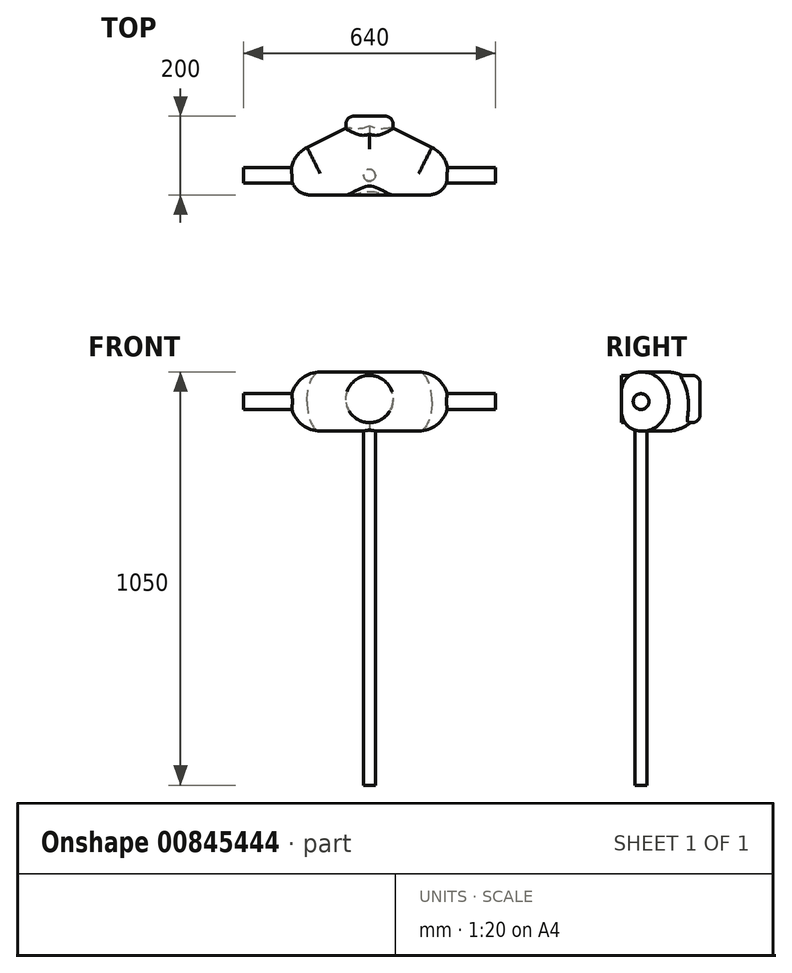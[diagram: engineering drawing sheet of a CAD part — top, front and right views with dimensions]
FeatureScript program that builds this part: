
annotation { "Feature Type Name" : "Feature", "Feature Type Description" : "" }
export const myFeature = defineFeature(function(context is Context, id is Id, definition is map)
    precondition{}
    {
        {
            var Q0;
            Q0=qCreatedBy(makeId("Top.planeOp"),FACE);
            var sketch = newSketch(context, id + "F0", { "sketchPlane" : qUnion([Q0])});
            skLineSegment(sketch, "E0.top", {"start": v(-200, 0) * mm, "end": v(200, 0) * mm});
            skLineSegment(sketch, "E0.left", {"start": v(-200, 100) * mm, "end": v(-200, 0) * mm});
            skLineSegment(sketch, "E0.right", {"start": v(200, 100) * mm, "end": v(200, 0) * mm});
            skLineSegment(sketch, "E1", {"start": v(-200, 100) * mm, "end": v(0, 200) * mm});
            skLineSegment(sketch, "E2", {"start": v(0, 200) * mm, "end": v(200, 100) * mm});
            skPoint(sketch, "E3.orphan", {"position": v(-200, 200) * mm});
            skPoint(sketch, "E4.orphan", {"position": v(200, 200) * mm});
            skSolve(sketch);
        }
        {
            var Q0;
            Q0=makeQuery(id+"F0.imprint","IMPRINT",FACE,{"disambiguationData":[TD([[makeQuery(id+"F0.imprint","IMPRINT",EDGE,{"derivedFrom":sQuery(id+"F0.wireOp",EDGE,"E0.top")}),1.0]])]});
            extrude(context, id + "F1", {"entities" : qUnion([Q0]), "depth" : 150 * mm, "offsetDistance" : 25 * mm});
        }
        {
            var Q0;
            Q0=makeQuery(id+"F1.opExtrude","SWEPT_FACE",FACE,{"disambiguationData":[OSD([sQuery(id+"F0.wireOp",EDGE,"E0.right")])]});
            var sketch = newSketch(context, id + "F2", { "sketchPlane" : qUnion([Q0])});
            skCircle(sketch, "E5", {"center": v(50, 75) * mm, "radius": 20 * mm});
            skSolve(sketch);
        }
        {
            var Q0;
            Q0=makeQuery(id+"F2.imprint","IMPRINT",FACE,{"disambiguationData":[TD([[makeQuery(id+"F2.imprint","IMPRINT",EDGE,{"derivedFrom":sQuery(id+"F2.wireOp",EDGE,"E5")}),1.0]])]});
            extrude(context, id + "F3", {"entities" : qUnion([Q0]), "operationType" : NewBodyOperationType.ADD, "depth" : 120 * mm, "offsetDistance" : 25 * mm});
        }
        {
            var Q0;
            Q0=makeQuery(id+"F1.opExtrude","SWEPT_FACE",FACE,{"disambiguationData":[OSD([sQuery(id+"F0.wireOp",EDGE,"E0.left")])]});
            var sketch = newSketch(context, id + "F4", { "sketchPlane" : qUnion([Q0])});
            skCircle(sketch, "E6", {"center": v(-50, 75) * mm, "radius": 20 * mm});
            skSolve(sketch);
        }
        {
            var Q0;
            Q0=makeQuery(id+"F4.imprint","IMPRINT",FACE,{"disambiguationData":[TD([[makeQuery(id+"F4.imprint","IMPRINT",EDGE,{"derivedFrom":sQuery(id+"F4.wireOp",EDGE,"E6")}),1.0]])]});
            extrude(context, id + "F5", {"entities" : qUnion([Q0]), "operationType" : NewBodyOperationType.ADD, "depth" : 120 * mm, "offsetDistance" : 25 * mm});
        }
        {
            var Q0;
            Q0=makeQuery(id+"F1.opExtrude","CAP_EDGE",EDGE,{"disambiguationData":[OSD([sQuery(id+"F0.wireOp",EDGE,"E2")])],"isStart":false});
            var Q1;
            Q1=makeQuery(id+"F1.opExtrude","CAP_EDGE",EDGE,{"disambiguationData":[OSD([sQuery(id+"F0.wireOp",EDGE,"E1")])],"isStart":false});
            fillet(context, id + "F6", {"entities" : qUnion([Q0, Q1]), "radius" : 75 * mm, "tangentPropagation" : true, "allowEdgeOverflow" : false});
        }
        {
            var Q0;
            Q0=qCreatedBy(makeId("Top.planeOp"),FACE);
            cPlane(context, id + "F7", {"entities" : qUnion([Q0]), "cplaneType" : CPlaneType.OFFSET, "offset" : 75 * mm, "width" : 150 * mm, "height" : 150 * mm});
        }
        {
            var Q0;
            Q0=qCreatedBy(id+"F7.planeOp",FACE);
            var sketch = newSketch(context, id + "F8", { "sketchPlane" : qUnion([Q0])});
            skFitSpline(sketch, "E7", {"points": [v(201.23, 72.54) * mm, v(229.73, 89.81) * mm, v(272.48, 86.79) * mm, v(312.64, 95.86) * mm], "startDerivative": vector(84.68, 74.54) * mm, "endDerivative": vector(113.81, 40.36) * mm});
            skSolve(sketch);
        }
        {
            var Q0;
            Q0=makeQuery(id+"F1.opExtrude","SWEPT_FACE",FACE,{"disambiguationData":[OSD([sQuery(id+"F0.wireOp",EDGE,"E0.right")])]});
            var sketch = newSketch(context, id + "F9", { "sketchPlane" : qUnion([Q0])});
            skCircle(sketch, "E8", {"center": v(72.54, 75) * mm, "radius": 2.5 * mm});
            skSolve(sketch);
        }
        {
            var Q0;
            Q0=makeQuery(id+"F1.opExtrude","SWEPT_EDGE",EDGE,{"disambiguationData":[OSD([sQuery(id+"F0.wireOp",EDGE,"E0.right"),sQuery(id+"F0.wireOp",EDGE,"E2")])]});
            var Q1;
            Q1=makeQuery(id+"F1.opExtrude","SWEPT_EDGE",EDGE,{"disambiguationData":[OSD([sQuery(id+"F0.wireOp",EDGE,"E0.left"),sQuery(id+"F0.wireOp",EDGE,"E1")])]});
            fillet(context, id + "F10", {"entities" : qUnion([Q0, Q1]), "radius" : 75 * mm, "tangentPropagation" : true, "allowEdgeOverflow" : false});
        }
        {
            var Q0;
            Q0=makeQuery(id+"F1.opExtrude","CAP_FACE",FACE,{"disambiguationData":[OSD([sQuery(id+"F0.wireOp",EDGE,"E0.top"),sQuery(id+"F0.wireOp",EDGE,"E0.left"),sQuery(id+"F0.wireOp",EDGE,"E0.right"),sQuery(id+"F0.wireOp",EDGE,"E1"),sQuery(id+"F0.wireOp",EDGE,"E2")])],"isStart":true});
            var sketch = newSketch(context, id + "F11", { "sketchPlane" : qUnion([Q0])});
            skCircle(sketch, "E9", {"center": v(0, -50) * mm, "radius": 15 * mm});
            skSolve(sketch);
        }
        {
            var Q0;
            Q0=makeQuery(id+"F11.imprint","IMPRINT",FACE,{"disambiguationData":[TD([[makeQuery(id+"F11.imprint","IMPRINT",EDGE,{"derivedFrom":sQuery(id+"F11.wireOp",EDGE,"E9")}),1.0]])]});
            extrude(context, id + "F12", {"entities" : qUnion([Q0]), "operationType" : NewBodyOperationType.ADD, "depth" : 900 * mm, "offsetDistance" : 25 * mm});
        }
        {
            var Q0;
            Q0=makeQuery(id+"F1.opExtrude","CAP_EDGE",EDGE,{"disambiguationData":[OSD([sQuery(id+"F0.wireOp",EDGE,"E2")])],"isStart":true});
            var Q1;
            {var subQ0=sQuery(id+"F0.wireOp",EDGE,"E2");var subQ1=sQuery(id+"F0.wireOp",EDGE,"E0.right");Q1=makeQuery(id+"F10.opFillet","BLEND_EDGE",EDGE,{"blendedFrom":[makeQuery(id+"F1.opExtrude","SWEPT_EDGE",EDGE,{"disambiguationData":[OSD([subQ1,subQ0])]}),makeQuery(id+"F1.opExtrude","CAP_FACE",FACE,{"disambiguationData":[OSD([sQuery(id+"F0.wireOp",EDGE,"E0.top"),sQuery(id+"F0.wireOp",EDGE,"E0.left"),subQ1,sQuery(id+"F0.wireOp",EDGE,"E1"),subQ0])],"isStart":true})],"blendedInto":[makeQuery(id+"F1.opExtrude","CAP_FACE",FACE,{"disambiguationData":[OSD([sQuery(id+"F0.wireOp",EDGE,"E0.top"),sQuery(id+"F0.wireOp",EDGE,"E0.left"),subQ1,sQuery(id+"F0.wireOp",EDGE,"E1"),subQ0])],"isStart":true})]});}
            var Q2;
            Q2=makeQuery(id+"F1.opExtrude","CAP_EDGE",EDGE,{"disambiguationData":[OSD([sQuery(id+"F0.wireOp",EDGE,"E0.right")])],"isStart":true});
            var Q3;
            Q3=makeQuery(id+"F1.opExtrude","CAP_EDGE",EDGE,{"disambiguationData":[OSD([sQuery(id+"F0.wireOp",EDGE,"E1")])],"isStart":true});
            var Q4;
            {var subQ0=sQuery(id+"F0.wireOp",EDGE,"E1");var subQ1=sQuery(id+"F0.wireOp",EDGE,"E0.left");Q4=makeQuery(id+"F10.opFillet","BLEND_EDGE",EDGE,{"blendedFrom":[makeQuery(id+"F1.opExtrude","SWEPT_EDGE",EDGE,{"disambiguationData":[OSD([subQ1,subQ0])]}),makeQuery(id+"F1.opExtrude","CAP_FACE",FACE,{"disambiguationData":[OSD([sQuery(id+"F0.wireOp",EDGE,"E0.top"),subQ1,sQuery(id+"F0.wireOp",EDGE,"E0.right"),subQ0,sQuery(id+"F0.wireOp",EDGE,"E2")])],"isStart":true})],"blendedInto":[makeQuery(id+"F1.opExtrude","CAP_FACE",FACE,{"disambiguationData":[OSD([sQuery(id+"F0.wireOp",EDGE,"E0.top"),subQ1,sQuery(id+"F0.wireOp",EDGE,"E0.right"),subQ0,sQuery(id+"F0.wireOp",EDGE,"E2")])],"isStart":true})]});}
            var Q5;
            Q5=makeQuery(id+"F1.opExtrude","CAP_EDGE",EDGE,{"disambiguationData":[OSD([sQuery(id+"F0.wireOp",EDGE,"E0.left")])],"isStart":true});
            fillet(context, id + "F13", {"entities" : qUnion([Q0, Q1, Q2, Q3, Q4, Q5]), "radius" : 75 * mm, "tangentPropagation" : true, "allowEdgeOverflow" : false});
        }
        {
            var Q0;
            Q0=makeQuery(id+"F1.opExtrude","CAP_EDGE",EDGE,{"disambiguationData":[OSD([sQuery(id+"F0.wireOp",EDGE,"E0.top")])],"isStart":false});
            var Q1;
            Q1=makeQuery(id+"F10.opFillet","BLEND_EDGE",EDGE,{"blendedFrom":[makeQuery(id+"F1.opExtrude","CAP_EDGE",EDGE,{"disambiguationData":[OSD([sQuery(id+"F0.wireOp",EDGE,"E0.right")])],"isStart":false}),makeQuery(id+"F1.opExtrude","SWEPT_FACE",FACE,{"disambiguationData":[OSD([sQuery(id+"F0.wireOp",EDGE,"E0.top")])]})],"blendedInto":[makeQuery(id+"F1.opExtrude","SWEPT_FACE",FACE,{"disambiguationData":[OSD([sQuery(id+"F0.wireOp",EDGE,"E0.top")])]})]});
            var Q2;
            Q2=makeQuery(id+"F13.opFillet","BLEND_EDGE",EDGE,{"blendedFrom":[makeQuery(id+"F1.opExtrude","CAP_EDGE",EDGE,{"disambiguationData":[OSD([sQuery(id+"F0.wireOp",EDGE,"E0.right")])],"isStart":true}),makeQuery(id+"F1.opExtrude","SWEPT_FACE",FACE,{"disambiguationData":[OSD([sQuery(id+"F0.wireOp",EDGE,"E0.top")])]})],"blendedInto":[makeQuery(id+"F1.opExtrude","SWEPT_FACE",FACE,{"disambiguationData":[OSD([sQuery(id+"F0.wireOp",EDGE,"E0.top")])]})]});
            var Q3;
            Q3=makeQuery(id+"F1.opExtrude","CAP_EDGE",EDGE,{"disambiguationData":[OSD([sQuery(id+"F0.wireOp",EDGE,"E0.top")])],"isStart":true});
            var Q4;
            Q4=makeQuery(id+"F13.opFillet","BLEND_EDGE",EDGE,{"blendedFrom":[makeQuery(id+"F1.opExtrude","CAP_EDGE",EDGE,{"disambiguationData":[OSD([sQuery(id+"F0.wireOp",EDGE,"E0.left")])],"isStart":true}),makeQuery(id+"F1.opExtrude","SWEPT_FACE",FACE,{"disambiguationData":[OSD([sQuery(id+"F0.wireOp",EDGE,"E0.top")])]})],"blendedInto":[makeQuery(id+"F1.opExtrude","SWEPT_FACE",FACE,{"disambiguationData":[OSD([sQuery(id+"F0.wireOp",EDGE,"E0.top")])]})]});
            var Q5;
            Q5=makeQuery(id+"F10.opFillet","BLEND_EDGE",EDGE,{"blendedFrom":[makeQuery(id+"F1.opExtrude","CAP_EDGE",EDGE,{"disambiguationData":[OSD([sQuery(id+"F0.wireOp",EDGE,"E0.left")])],"isStart":false}),makeQuery(id+"F1.opExtrude","SWEPT_FACE",FACE,{"disambiguationData":[OSD([sQuery(id+"F0.wireOp",EDGE,"E0.top")])]})],"blendedInto":[makeQuery(id+"F1.opExtrude","SWEPT_FACE",FACE,{"disambiguationData":[OSD([sQuery(id+"F0.wireOp",EDGE,"E0.top")])]})]});
            fillet(context, id + "F14", {"entities" : qUnion([Q0, Q1, Q2, Q3, Q4, Q5]), "radius" : 50 * mm, "tangentPropagation" : true, "allowEdgeOverflow" : false});
        }
        {
            var Q0;
            Q0=makeQuery(id+"F1.opExtrude","SWEPT_FACE",FACE,{"disambiguationData":[OSD([sQuery(id+"F0.wireOp",EDGE,"E0.top")])]});
            var sketch = newSketch(context, id + "F15", { "sketchPlane" : qUnion([Q0])});
            skCircle(sketch, "E10", {"center": v(0, 81.49) * mm, "radius": 59.99 * mm});
            skSolve(sketch);
        }
        {
            var Q0;
            Q0 = qSketchRegion(id + "F15", true);
            extrude(context, id + "F16", {"entities" : qUnion([Q0]), "operationType" : NewBodyOperationType.ADD, "oppositeDirection" : true, "depth" : 200 * mm, "offsetDistance" : 25 * mm});
        }
        {
            var Q0;
            Q0=makeQuery(id+"F16.opExtrude","CAP_FACE",FACE,{"disambiguationData":[OSD([sQuery(id+"F15.wireOp",EDGE,"E10")])],"isStart":false});
            fillet(context, id + "F17", {"entities" : qUnion([Q0]), "radius" : 20 * mm, "tangentPropagation" : true, "allowEdgeOverflow" : false});
        }
    });
